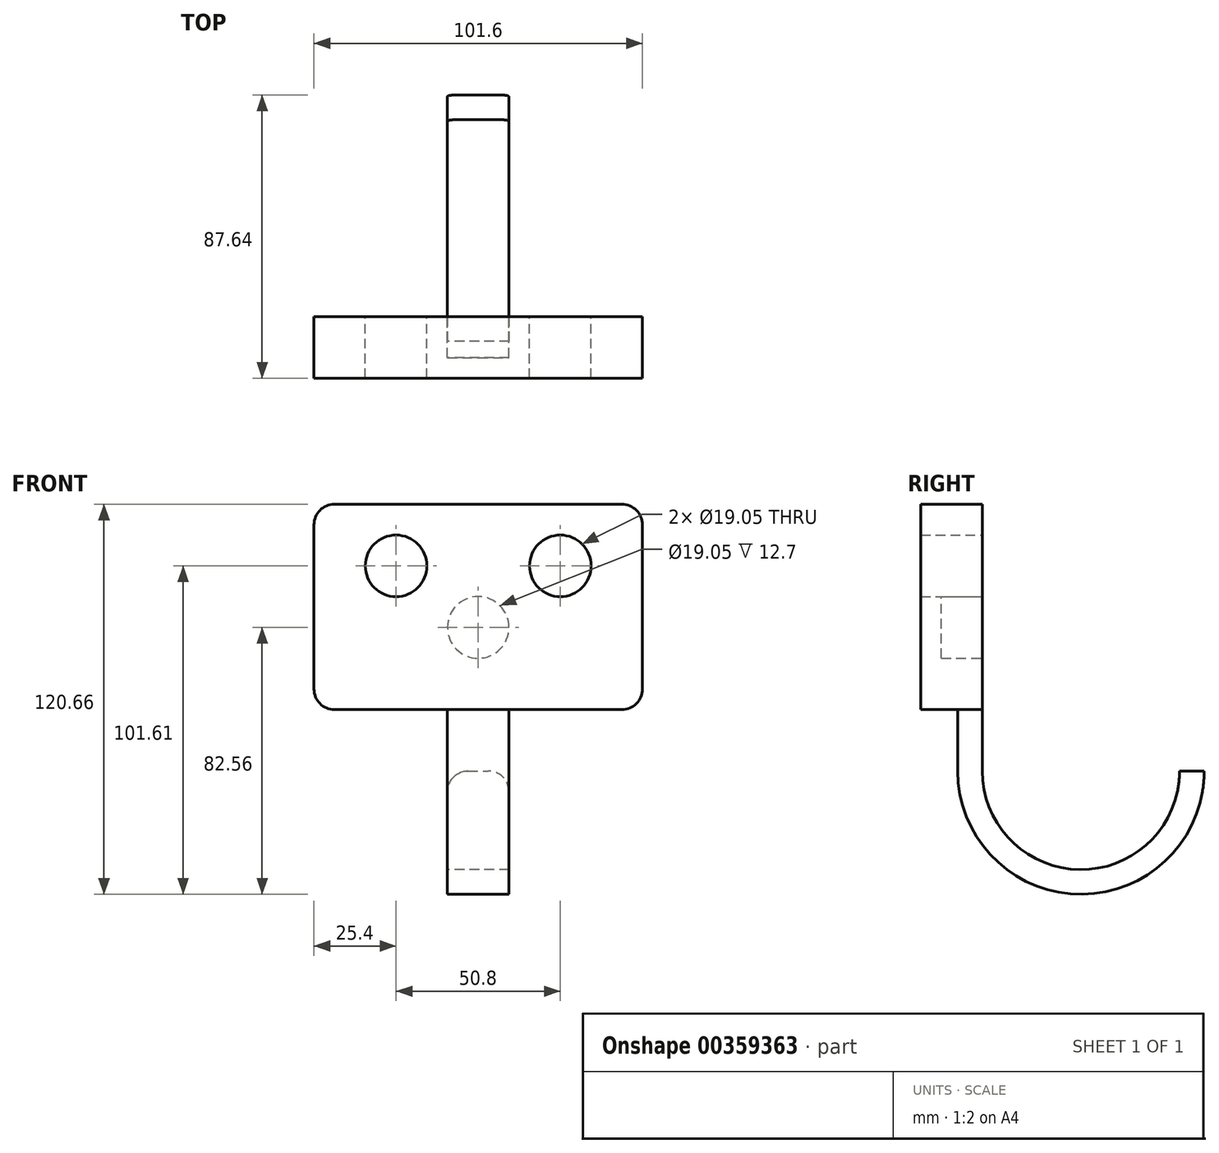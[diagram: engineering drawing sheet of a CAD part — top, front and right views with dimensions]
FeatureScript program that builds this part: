
annotation { "Feature Type Name" : "Feature", "Feature Type Description" : "" }
export const myFeature = defineFeature(function(context is Context, id is Id, definition is map)
    precondition{}
    {
        {
            var Q0;
            Q0=qCreatedBy(makeId("Front.planeOp"),FACE);
            var sketch = newSketch(context, id + "F0", { "sketchPlane" : qUnion([Q0])});
            skLineSegment(sketch, "E0.bottom", {"start": v(50.8, 31.75) * mm, "end": v(-50.8, 31.75) * mm});
            skLineSegment(sketch, "E0.top", {"start": v(50.8, -31.75) * mm, "end": v(-50.8, -31.75) * mm});
            skLineSegment(sketch, "E0.left", {"start": v(50.8, 31.75) * mm, "end": v(50.8, -31.75) * mm});
            skLineSegment(sketch, "E0.right", {"start": v(-50.8, 31.75) * mm, "end": v(-50.8, -31.75) * mm});
            skPoint(sketch, "E0.middle", {"position": v(0, 0) * mm});
            skLineSegment(sketch, "E1", {"start": v(-9.52, -31.75) * mm, "end": v(-9.52, -50.8) * mm});
            skLineSegment(sketch, "E2", {"start": v(9.52, -31.75) * mm, "end": v(9.52, -50.8) * mm});
            skLineSegment(sketch, "E3", {"start": v(-9.52, -50.8) * mm, "end": v(9.52, -50.8) * mm});
            skSolve(sketch);
        }
        {
            var Q0;
            Q0=makeQuery(id+"F0.imprint","IMPRINT",FACE,{"disambiguationData":[TD([[makeQuery(id+"F0.imprint","IMPRINT",EDGE,{"derivedFrom":sQuery(id+"F0.wireOp",EDGE,"E0.bottom")}),1.0]])]});
            extrude(context, id + "F1", {"entities" : qUnion([Q0]), "depth" : 19.05 * mm});
        }
        {
            var Q0;
            Q0=makeQuery(id+"F1.opExtrude","SWEPT_EDGE",EDGE,{"disambiguationData":[OSD([sQuery(id+"F0.wireOp",EDGE,"E0.bottom"),sQuery(id+"F0.wireOp",EDGE,"E0.left")])]});
            var Q1;
            Q1=makeQuery(id+"F1.opExtrude","SWEPT_EDGE",EDGE,{"disambiguationData":[OSD([sQuery(id+"F0.wireOp",EDGE,"E0.top"),sQuery(id+"F0.wireOp",EDGE,"E0.left")])]});
            var Q2;
            Q2=makeQuery(id+"F1.opExtrude","SWEPT_EDGE",EDGE,{"disambiguationData":[OSD([sQuery(id+"F0.wireOp",EDGE,"E0.top"),sQuery(id+"F0.wireOp",EDGE,"E0.right")])]});
            var Q3;
            Q3=makeQuery(id+"F1.opExtrude","SWEPT_EDGE",EDGE,{"disambiguationData":[OSD([sQuery(id+"F0.wireOp",EDGE,"E0.bottom"),sQuery(id+"F0.wireOp",EDGE,"E0.right")])]});
            fillet(context, id + "F2", {"entities" : qUnion([Q0, Q1, Q2, Q3]), "radius" : 6.35 * mm, "tangentPropagation" : true, "allowEdgeOverflow" : false});
        }
        {
            var Q0;
            {var subQ0=sQuery(id+"F0.wireOp",EDGE,"E1");Q0=makeQuery(id+"F0.imprint","IMPRINT",FACE,{"disambiguationData":[TD([[makeQuery(id+"F0.imprint","IMPRINT",EDGE,{"derivedFrom":subQ0}),1.0]])]});}
            extrude(context, id + "F3", {"entities" : qUnion([Q0]), "operationType" : NewBodyOperationType.ADD, "depth" : 7.62 * mm});
        }
        {
            var Q0;
            Q0=makeQuery(id+"F3.opExtrude","SWEPT_FACE",FACE,{"disambiguationData":[OSD([sQuery(id+"F0.wireOp",EDGE,"E3")])]});
            var sketch = newSketch(context, id + "F4", { "sketchPlane" : qUnion([Q0])});
            skLineSegment(sketch, "E4", {"start": v(19.42, -30.49) * mm, "end": v(-27.65, -30.49) * mm});
            skSolve(sketch);
        }
        {
            var Q0;
            {var subQ0=sQuery(id+"F0.wireOp",EDGE,"E3");Q0=makeQuery(id+"F4.imprint","IMPRINT",FACE,{"disambiguationData":[TD([[makeQuery(id+"F4.imprint","IMPRINT",EDGE,{"derivedFrom":makeQuery(id+"F3.opExtrude","CAP_EDGE",EDGE,{"disambiguationData":[OSD([subQ0])],"isStart":true})}),1.0]])]});}
            var Q1;
            Q1=sQuery(id+"F4.wireOp",EDGE,"E4");
            revolve(context, id + "F5", {"operationType" : NewBodyOperationType.ADD, "entities" : qUnion([Q0]), "axis" : qUnion([Q1]), "revolveType" : RevolveType.ONE_DIRECTION, "oppositeDirection" : true, "angle" : 180 * degree});
        }
        {
            var Q0;
            Q0=makeQuery(id+"F5.opRevolve","CAP_EDGE",EDGE,{"disambiguationData":[OSD([sQuery(id+"F0.wireOp",EDGE,"E1"),sQuery(id+"F0.wireOp",EDGE,"E3")])],"isStart":false});
            var Q1;
            Q1=makeQuery(id+"F5.opRevolve","CAP_EDGE",EDGE,{"disambiguationData":[OSD([sQuery(id+"F0.wireOp",EDGE,"E2"),sQuery(id+"F0.wireOp",EDGE,"E3")])],"isStart":false});
            fillet(context, id + "F6", {"entities" : qUnion([Q0, Q1]), "radius" : 6.35 * mm, "tangentPropagation" : true, "allowEdgeOverflow" : false});
        }
        {
            var Q0;
            Q0=makeQuery(id+"F0.imprint","IMPRINT",FACE,{"disambiguationData":[TD([[makeQuery(id+"F0.imprint","IMPRINT",EDGE,{"derivedFrom":sQuery(id+"F0.wireOp",EDGE,"E0.bottom")}),1.0]])]});
            var sketch = newSketch(context, id + "F7", { "sketchPlane" : qUnion([Q0])});
            skCircle(sketch, "E5", {"center": v(-25.4, 12.7) * mm, "radius": 9.53 * mm});
            skCircle(sketch, "E6", {"center": v(25.4, 12.7) * mm, "radius": 9.53 * mm});
            skSolve(sketch);
        }
        {
            var Q0;
            Q0 = qSketchRegion(id + "F7", true);
            extrude(context, id + "F8", {"entities" : qUnion([Q0]), "operationType" : NewBodyOperationType.REMOVE, "endBound" : BoundingType.THROUGH_ALL, "depth" : 25.4 * mm});
        }
        {
            var Q0;
            Q0=makeQuery(id+"F0.imprint","IMPRINT",FACE,{"disambiguationData":[TD([[makeQuery(id+"F0.imprint","IMPRINT",EDGE,{"derivedFrom":sQuery(id+"F0.wireOp",EDGE,"E0.bottom")}),1.0]])]});
            var sketch = newSketch(context, id + "F9", { "sketchPlane" : qUnion([Q0])});
            skCircle(sketch, "E7", {"center": v(0, -6.35) * mm, "radius": 9.53 * mm});
            skSolve(sketch);
        }
        {
            var Q0;
            Q0 = qSketchRegion(id + "F9", true);
            extrude(context, id + "F10", {"entities" : qUnion([Q0]), "operationType" : NewBodyOperationType.REMOVE, "depth" : 12.7 * mm});
        }
    });
